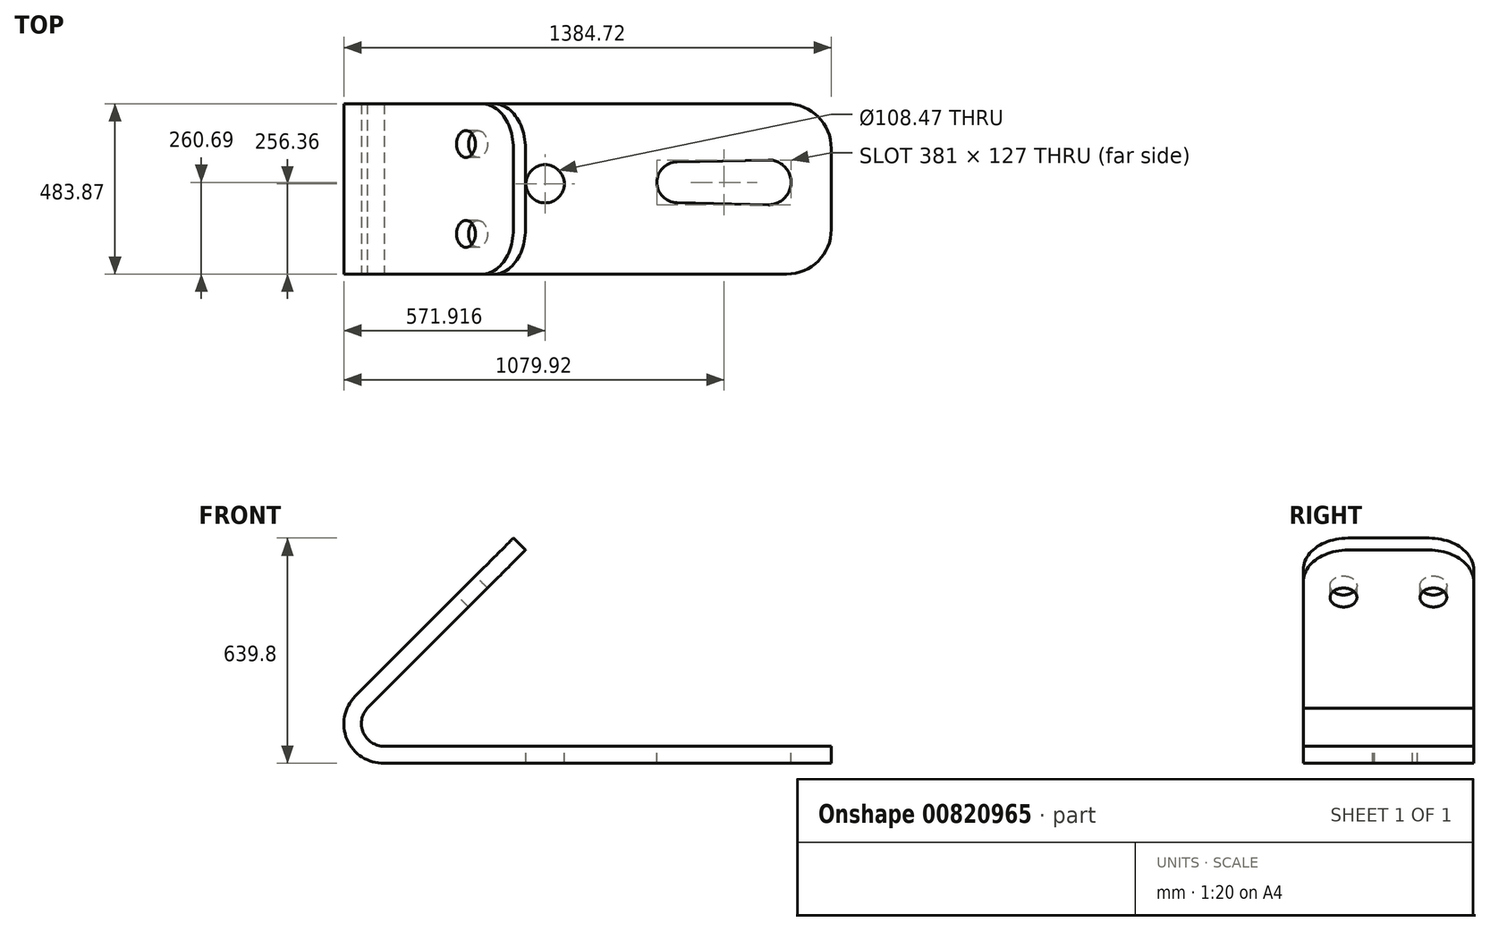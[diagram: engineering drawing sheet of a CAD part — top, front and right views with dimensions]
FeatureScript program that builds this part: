
annotation { "Feature Type Name" : "Feature", "Feature Type Description" : "" }
export const myFeature = defineFeature(function(context is Context, id is Id, definition is map)
    precondition{}
    {
        {
            var Q0;
            Q0=qCreatedBy(makeId("Front.planeOp"),FACE);
            var sketch = newSketch(context, id + "F0", { "sketchPlane" : qUnion([Q0])});
            skLineSegment(sketch, "E0", {"start": v(604.1, -27.51) * mm, "end": v(604.1, -75.77) * mm});
            skLineSegment(sketch, "E1", {"start": v(604.1, -75.77) * mm, "end": v(-665.9, -75.77) * mm});
            skLineSegment(sketch, "E2", {"start": v(-665.9, -27.51) * mm, "end": v(604.1, -27.51) * mm});
            skLineSegment(sketch, "E3", {"start": v(-713.76, 80.85) * mm, "end": v(-264.75, 529.86) * mm});
            skLineSegment(sketch, "E4", {"start": v(-264.75, 529.86) * mm, "end": v(-298.87, 563.99) * mm});
            skLineSegment(sketch, "E5", {"start": v(-298.87, 563.99) * mm, "end": v(-747.89, 114.98) * mm});
            skArc(sketch, "E6", {"start": v(-713.76, 80.85) * mm, "mid": v(-725.13, 11.08) * mm, "end": v(-665.9, -27.51) * mm});
            skArc(sketch, "E7", {"start": v(-747.89, 114.98) * mm, "mid": v(-771.54, -8.18) * mm, "end": v(-665.9, -75.77) * mm});
            skSolve(sketch);
        }
        {
            var Q0;
            Q0=makeQuery(id+"F0.imprint","IMPRINT",FACE,{"disambiguationData":[TD([[makeQuery(id+"F0.imprint","IMPRINT",EDGE,{"derivedFrom":sQuery(id+"F0.wireOp",EDGE,"E0")}),-1.0]])]});
            extrude(context, id + "F1", {"entities" : qUnion([Q0]), "oppositeDirection" : true, "depth" : 483.87 * mm, "offsetDistance" : 25.4 * mm});
        }
        {
            var Q0;
            Q0=makeQuery(id+"F1.opExtrude","CAP_EDGE",EDGE,{"disambiguationData":[OSD([sQuery(id+"F0.wireOp",EDGE,"E0")])],"isStart":false});
            var Q1;
            Q1=makeQuery(id+"F1.opExtrude","CAP_EDGE",EDGE,{"disambiguationData":[OSD([sQuery(id+"F0.wireOp",EDGE,"E0")])],"isStart":true});
            fillet(context, id + "F2", {"entities" : qUnion([Q0, Q1]), "radius" : 127 * mm, "tangentPropagation" : true, "allowEdgeOverflow" : false});
        }
        {
            var Q0;
            Q0=makeQuery(id+"F1.opExtrude","SWEPT_FACE",FACE,{"disambiguationData":[OSD([sQuery(id+"F0.wireOp",EDGE,"E2")])]});
            var sketch = newSketch(context, id + "F3", { "sketchPlane" : qUnion([Q0])});
            skCircle(sketch, "E8", {"center": v(-208.7, 256.36) * mm, "radius": 54.23 * mm});
            skLineSegment(sketch, "E9", {"start": v(165.5, 318.63) * mm, "end": v(424.92, 324.19) * mm});
            skArc(sketch, "E10", {"start": v(165.5, 318.63) * mm, "mid": v(108.8, 260.69) * mm, "end": v(165.5, 202.75) * mm});
            skLineSegment(sketch, "E11", {"start": v(165.5, 202.75) * mm, "end": v(424.92, 197.19) * mm});
            skArc(sketch, "E12", {"start": v(424.92, 197.19) * mm, "mid": v(489.8, 260.69) * mm, "end": v(424.92, 324.19) * mm});
            skSolve(sketch);
        }
        {
            var Q0;
            Q0=makeQuery(id+"F3.imprint","IMPRINT",FACE,{"disambiguationData":[TD([[makeQuery(id+"F3.imprint","IMPRINT",EDGE,{"derivedFrom":sQuery(id+"F3.wireOp",EDGE,"E9")}),-1.0]])]});
            var Q1;
            Q1=makeQuery(id+"F3.imprint","IMPRINT",FACE,{"disambiguationData":[TD([[makeQuery(id+"F3.imprint","IMPRINT",EDGE,{"derivedFrom":sQuery(id+"F3.wireOp",EDGE,"E8")}),1.0]])]});
            extrude(context, id + "F4", {"entities" : qUnion([Q0, Q1]), "operationType" : NewBodyOperationType.REMOVE, "endBound" : BoundingType.THROUGH_ALL, "oppositeDirection" : true, "depth" : 25.4 * mm, "offsetDistance" : 25.4 * mm});
        }
        {
            var Q0;
            Q0=makeQuery(id+"F1.opExtrude","CAP_EDGE",EDGE,{"disambiguationData":[OSD([sQuery(id+"F0.wireOp",EDGE,"E4")])],"isStart":false});
            var Q1;
            Q1=makeQuery(id+"F1.opExtrude","CAP_EDGE",EDGE,{"disambiguationData":[OSD([sQuery(id+"F0.wireOp",EDGE,"E4")])],"isStart":true});
            fillet(context, id + "F5", {"entities" : qUnion([Q0, Q1]), "radius" : 127 * mm, "tangentPropagation" : true, "allowEdgeOverflow" : false});
        }
        {
            var Q0;
            Q0=makeQuery(id+"F1.opExtrude","SWEPT_FACE",FACE,{"disambiguationData":[OSD([sQuery(id+"F0.wireOp",EDGE,"E5")])]});
            var sketch = newSketch(context, id + "F6", { "sketchPlane" : qUnion([Q0])});
            skCircle(sketch, "E13", {"center": v(-369.57, -3.03) * mm, "radius": 38.1 * mm});
            skCircle(sketch, "E14", {"center": v(-114.3, -3.03) * mm, "radius": 38.1 * mm});
            skSolve(sketch);
        }
        {
            var Q0;
            Q0=makeQuery(id+"F6.imprint","IMPRINT",FACE,{"disambiguationData":[TD([[makeQuery(id+"F6.imprint","IMPRINT",EDGE,{"derivedFrom":sQuery(id+"F6.wireOp",EDGE,"E13")}),1.0]])]});
            var Q1;
            Q1=makeQuery(id+"F6.imprint","IMPRINT",FACE,{"disambiguationData":[TD([[makeQuery(id+"F6.imprint","IMPRINT",EDGE,{"derivedFrom":sQuery(id+"F6.wireOp",EDGE,"E14")}),1.0]])]});
            extrude(context, id + "F7", {"entities" : qUnion([Q0, Q1]), "operationType" : NewBodyOperationType.REMOVE, "oppositeDirection" : true, "depth" : 50.8 * mm, "offsetDistance" : 25.4 * mm});
        }
    });
